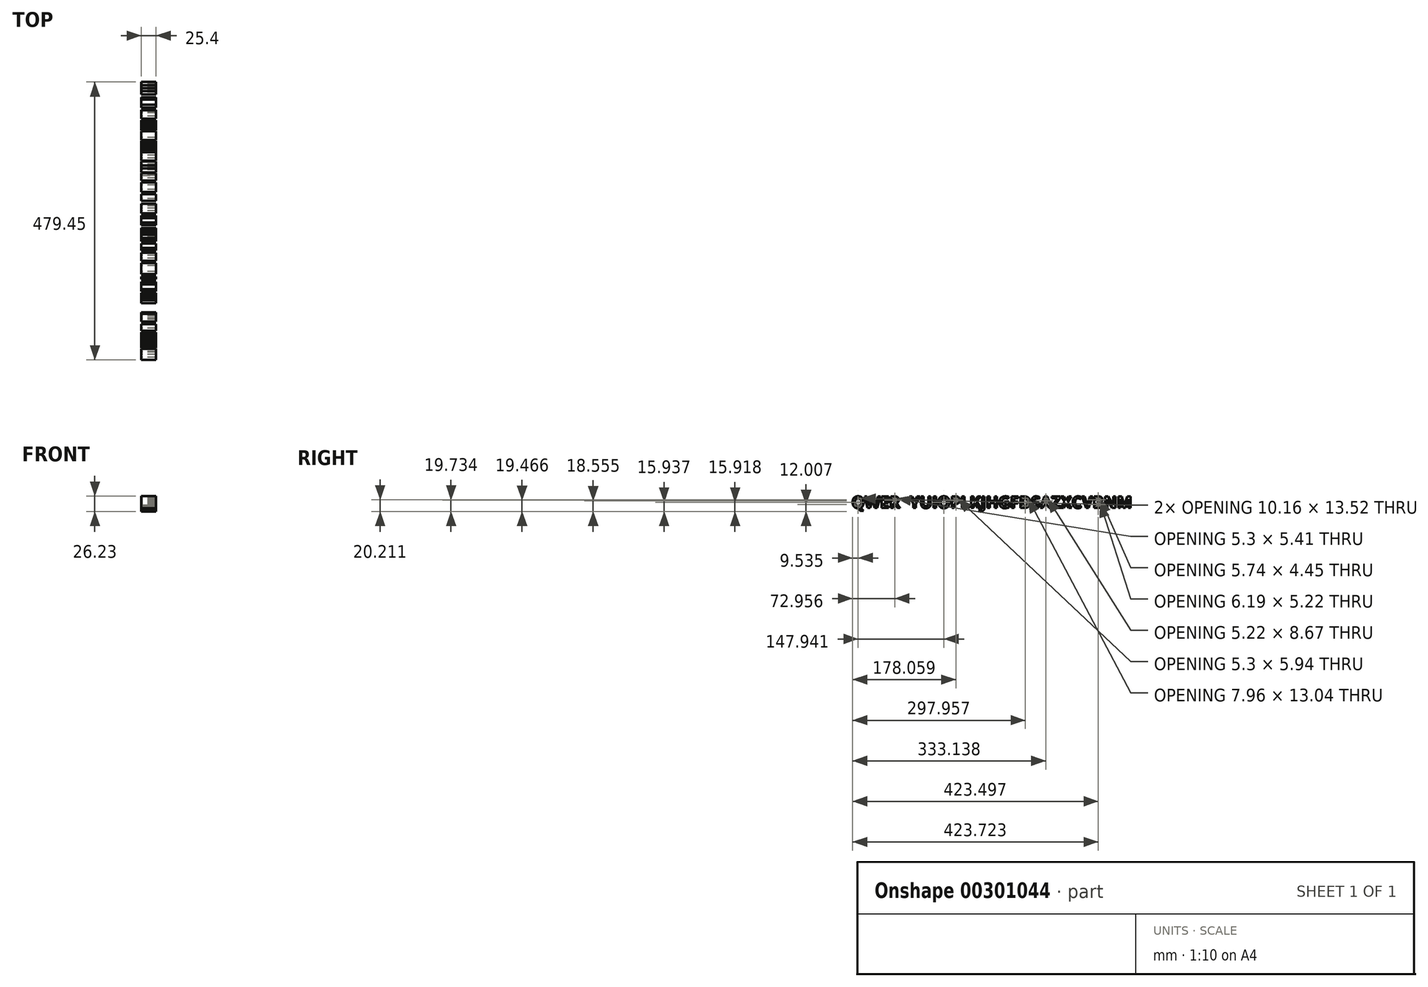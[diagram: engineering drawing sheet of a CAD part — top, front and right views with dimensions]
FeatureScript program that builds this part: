
annotation { "Feature Type Name" : "Feature", "Feature Type Description" : "" }
export const myFeature = defineFeature(function(context is Context, id is Id, definition is map)
    precondition{}
    {
        {
            var Q0;
            Q0=qCreatedBy(makeId("Right.planeOp"),FACE);
            var sketch = newSketch(context, id + "F0", { "sketchPlane" : qUnion([Q0])});
            skText(sketch, "E0", { "text": "QWERTYUIOPLKJHGFDSAZXCVBNM", "fontName": "OpenSans-Bold.ttf"});
            const initialGuessF0  = {"E0": [-0.06396, 0.03458, 1, 0, 0.0202]};
            skSetInitialGuess(sketch, initialGuessF0);
            skSolve(sketch);
        }
        {
            var Q0;
            Q0=qSketchRegion(id+"F0",true);
            extrude(context, id + "F1", {"entities" : qUnion([Q0]), "depth" : 25.4 * mm});
        }
        {
            var Q0;
            Q0=makeQuery(id+"F1.opExtrude","SWEPT_BODY",BODY,{"disambiguationData":[OSD([sQuery(id+"F0.wireOp",EDGE,"E0.sketch_text.stroke-73"),sQuery(id+"F0.wireOp",EDGE,"E0.sketch_text.stroke-74"),sQuery(id+"F0.wireOp",EDGE,"E0.sketch_text.stroke-75"),sQuery(id+"F0.wireOp",EDGE,"E0.sketch_text.stroke-76"),sQuery(id+"F0.wireOp",EDGE,"E0.sketch_text.stroke-77"),sQuery(id+"F0.wireOp",EDGE,"E0.sketch_text.stroke-78"),sQuery(id+"F0.wireOp",EDGE,"E0.sketch_text.stroke-79"),sQuery(id+"F0.wireOp",EDGE,"E0.sketch_text.stroke-80")])]});
            deleteBodies(context, id + "F2", {"entities" : qUnion([Q0])});
        }
    });
